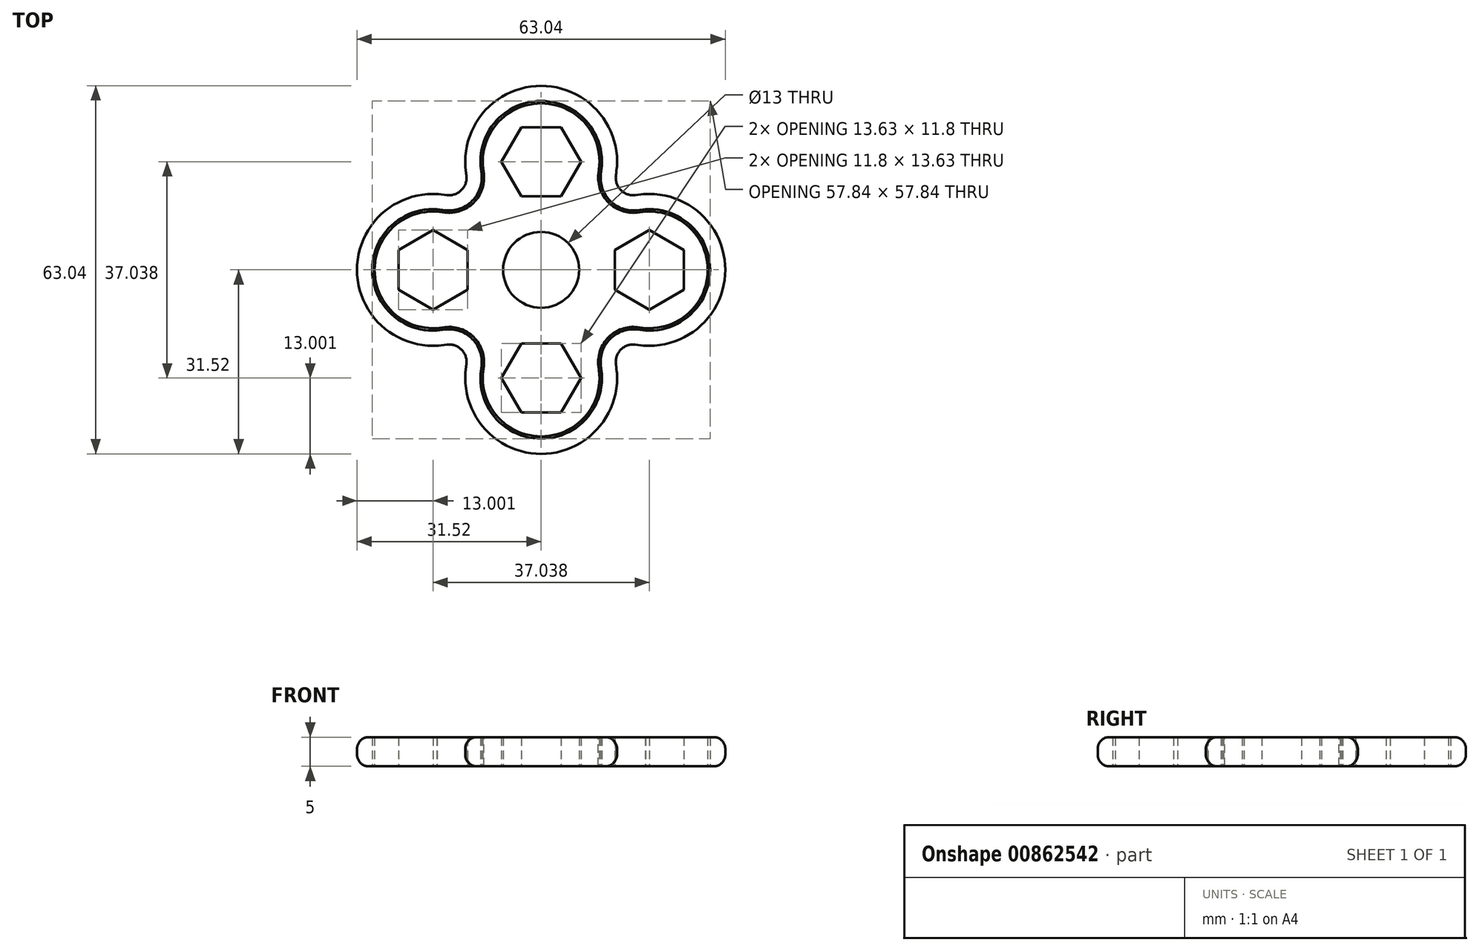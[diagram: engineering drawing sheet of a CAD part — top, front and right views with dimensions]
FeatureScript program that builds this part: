
annotation { "Feature Type Name" : "Feature", "Feature Type Description" : "" }
export const myFeature = defineFeature(function(context is Context, id is Id, definition is map)
    precondition{}
    {
        {
            var Q0;
            Q0=qCreatedBy(makeId("Top.planeOp"),FACE);
            var sketch = newSketch(context, id + "F0", { "sketchPlane" : qUnion([Q0])});
            skCircle(sketch, "E0", {"center": v(0, 0) * mm, "radius": 6.5 * mm});
            skPoint(sketch, "E1.0.midPoint", {"position": v(0, 12.5) * mm});
            skCircle(sketch, "E2.cCircle", {"center": v(0, 18.52) * mm, "radius": 10 * mm});
            skLineSegment(sketch, "E2.0", {"start": v(-5.77, 28.52) * mm, "end": v(5.77, 28.52) * mm});
            skLineSegment(sketch, "E2.1", {"start": v(5.77, 28.52) * mm, "end": v(11.55, 18.52) * mm, "construction": true});
            skLineSegment(sketch, "E2.2", {"start": v(11.55, 18.52) * mm, "end": v(5.77, 8.52) * mm, "construction": true});
            skLineSegment(sketch, "E2.3", {"start": v(5.77, 8.52) * mm, "end": v(-5.77, 8.52) * mm});
            skLineSegment(sketch, "E2.4", {"start": v(-5.77, 8.52) * mm, "end": v(-11.55, 18.52) * mm, "construction": true});
            skLineSegment(sketch, "E2.5", {"start": v(-11.55, 18.52) * mm, "end": v(-5.77, 28.52) * mm, "construction": true});
            skPoint(sketch, "E2.0.midPoint", {"position": v(0, 28.52) * mm});
            skCircle(sketch, "E3.cCircle", {"center": v(0, 18.52) * mm, "radius": 5.9 * mm, "construction": true});
            skLineSegment(sketch, "E3.0", {"start": v(-3.4, 24.42) * mm, "end": v(3.4, 24.42) * mm});
            skLineSegment(sketch, "E3.1", {"start": v(3.4, 24.42) * mm, "end": v(6.81, 18.52) * mm});
            skLineSegment(sketch, "E3.2", {"start": v(6.81, 18.52) * mm, "end": v(3.4, 12.62) * mm});
            skLineSegment(sketch, "E3.3", {"start": v(3.4, 12.62) * mm, "end": v(-3.4, 12.62) * mm});
            skLineSegment(sketch, "E3.4", {"start": v(-3.4, 12.62) * mm, "end": v(-6.81, 18.52) * mm});
            skLineSegment(sketch, "E3.5", {"start": v(-6.81, 18.52) * mm, "end": v(-3.4, 24.42) * mm});
            skPoint(sketch, "E3.0.midPoint", {"position": v(0, 24.42) * mm});
            skLineSegment(sketch, "E4", {"start": v(0, 8.52) * mm, "end": v(0, 12.5) * mm, "construction": true});
            skLineSegment(sketch, "E5", {"start": v(14.43, 0) * mm, "end": v(26.22, 0) * mm, "construction": true});
            skCircle(sketch, "E6.cCircle", {"center": v(0, 0) * mm, "radius": 12.62 * mm, "construction": true});
            skLineSegment(sketch, "E6.0", {"start": v(-5.23, 12.62) * mm, "end": v(5.23, 12.62) * mm});
            skLineSegment(sketch, "E6.1", {"start": v(5.23, 12.62) * mm, "end": v(12.62, 5.23) * mm});
            skLineSegment(sketch, "E6.2", {"start": v(12.62, 5.23) * mm, "end": v(12.62, -5.23) * mm});
            skLineSegment(sketch, "E6.3", {"start": v(12.62, -5.23) * mm, "end": v(5.23, -12.62) * mm});
            skLineSegment(sketch, "E6.4", {"start": v(5.23, -12.62) * mm, "end": v(-5.23, -12.62) * mm});
            skLineSegment(sketch, "E6.5", {"start": v(-5.23, -12.62) * mm, "end": v(-12.62, -5.23) * mm});
            skLineSegment(sketch, "E6.6", {"start": v(-12.62, -5.23) * mm, "end": v(-12.62, 5.23) * mm});
            skLineSegment(sketch, "E6.7", {"start": v(-12.62, 5.23) * mm, "end": v(-5.23, 12.62) * mm});
            skPoint(sketch, "E6.0.midPoint", {"position": v(0, 12.62) * mm});
            skLineSegment(sketch, "E7", {"start": v(-9.98, 17.86) * mm, "end": v(-8.92, 8.92) * mm});
            skLineSegment(sketch, "E8", {"start": v(8.92, 8.92) * mm, "end": v(9.98, 17.86) * mm});
            skSolve(sketch);
        }
        {
            var Q0;
            Q0=makeQuery(id+"F0.imprint","IMPRINT",FACE,{"disambiguationData":[TD([[makeQuery(id+"F0.imprint","IMPRINT",EDGE,{"derivedFrom":sQuery(id+"F0.wireOp",EDGE,"E0")}),-1.0]])]});
            var Q1;
            {var subQ1=sQuery(id+"F0.wireOp",EDGE,"E1.0");Q1=makeQuery(id+"F0.imprint","IMPRINT",FACE,{"disambiguationData":[TD([[makeQuery(id+"F0.imprint","IMPRINT",EDGE,{"derivedFrom":subQ1}),-1.0]])]});}
            extrude(context, id + "F1", {"entities" : qUnion([Q0, Q1]), "depth" : 5 * mm, "offsetDistance" : 25 * mm});
        }
        {
            var Q0;
            {var subQ5=sQuery(id+"F0.wireOp",EDGE,"E1.0");Q0=makeQuery(id+"F0.imprint","IMPRINT",FACE,{"disambiguationData":[TD([[makeQuery(id+"F0.imprint","IMPRINT",EDGE,{"derivedFrom":subQ5}),1.0]])]});}
            var Q1;
            {var subQ1=sQuery(id+"F0.wireOp",EDGE,"E1.0");Q1=makeQuery(id+"F0.imprint","IMPRINT",FACE,{"disambiguationData":[TD([[makeQuery(id+"F0.imprint","IMPRINT",EDGE,{"derivedFrom":subQ1}),-1.0]])]});}
            var Q2;
            {var subQ0=sQuery(id+"F0.wireOp",EDGE,"06393e6b-db47-430a-9c8e-1a9a39b87be70.MirrorC");var subQ1=sQuery(id+"F0.wireOp",EDGE,"E1.5");var subQ2=makeQuery(id+"F0.imprint","INTERSECT",VERTEX,{"derivedFrom":[subQ1,subQ0]});Q2=makeQuery(id+"F0.imprint","IMPRINT",FACE,{"disambiguationData":[TD([[makeQuery(id+"F0.imprint","IMPRINT",EDGE,{"disambiguationData":[TD([[subQ2,-1.0]])],"derivedFrom":subQ1}),1.0]])]});}
            var Q3;
            {var subQ0=sQuery(id+"F0.wireOp",EDGE,"rzDCEoio-iX78-1nDV-NMlx-LalMg3SrlLpn");var subQ1=sQuery(id+"F0.wireOp",EDGE,"E1.1");var subQ2=makeQuery(id+"F0.imprint","INTERSECT",VERTEX,{"derivedFrom":[subQ1,subQ0]});Q3=makeQuery(id+"F0.imprint","IMPRINT",FACE,{"disambiguationData":[TD([[makeQuery(id+"F0.imprint","IMPRINT",EDGE,{"disambiguationData":[TD([[subQ2,1.0]])],"derivedFrom":subQ1}),1.0]])]});}
            var Q4;
            Q4=makeQuery(id+"F0.imprint","IMPRINT",FACE,{"disambiguationData":[TD([[makeQuery(id+"F0.imprint","IMPRINT",EDGE,{"derivedFrom":sQuery(id+"F0.wireOp",EDGE,"E3.0")}),1.0]])]});
            var Q5;
            {var subQ0=sQuery(id+"F0.wireOp",EDGE,"E3.3");Q5=makeQuery(id+"F0.imprint","IMPRINT",FACE,{"disambiguationData":[TD([[makeQuery(id+"F0.imprint","IMPRINT",EDGE,{"derivedFrom":subQ0}),1.0]])]});}
            var Q6;
            {var subQ0=sQuery(id+"F0.wireOp",EDGE,"E7");var subQ1=sQuery(id+"F0.wireOp",EDGE,"E2.cCircle");var subQ2=makeQuery(id+"F0.imprint","INTERSECT",VERTEX,{"disambiguationData":[OD(0.0)],"derivedFrom":[subQ1,subQ0]});Q6=makeQuery(id+"F0.imprint","IMPRINT",FACE,{"disambiguationData":[TD([[makeQuery(id+"F0.imprint","IMPRINT",EDGE,{"disambiguationData":[TD([[subQ2,-1.0]])],"derivedFrom":subQ1}),-1.0]])]});}
            var Q7;
            {var subQ0=sQuery(id+"F0.wireOp",EDGE,"E6.1");var subQ1=sQuery(id+"F0.wireOp",EDGE,"E2.cCircle");var subQ2=makeQuery(id+"F0.imprint","INTERSECT",VERTEX,{"derivedFrom":[subQ1,subQ0]});Q7=makeQuery(id+"F0.imprint","IMPRINT",FACE,{"disambiguationData":[TD([[makeQuery(id+"F0.imprint","IMPRINT",EDGE,{"disambiguationData":[TD([[subQ2,-1.0]])],"derivedFrom":subQ1}),-1.0]])]});}
            extrude(context, id + "F2", {"entities" : qUnion([Q0, Q1, Q2, Q3, Q4, Q5, Q6, Q7]), "depth" : 5 * mm, "offsetDistance" : 25 * mm});
        }
        {
            var Q0;
            Q0=makeQuery(id+"F2.opExtrude","SWEPT_BODY",BODY,{"disambiguationData":[OSD([sQuery(id+"F0.wireOp",EDGE,"E2.cCircle"),sQuery(id+"F0.wireOp",EDGE,"E3.0"),sQuery(id+"F0.wireOp",EDGE,"E3.1"),sQuery(id+"F0.wireOp",EDGE,"E3.2"),sQuery(id+"F0.wireOp",EDGE,"E3.3"),sQuery(id+"F0.wireOp",EDGE,"E3.4"),sQuery(id+"F0.wireOp",EDGE,"E3.5"),sQuery(id+"F0.wireOp",EDGE,"E6.1"),sQuery(id+"F0.wireOp",EDGE,"E6.7"),sQuery(id+"F0.wireOp",EDGE,"E7"),sQuery(id+"F0.wireOp",EDGE,"E8")])]});
            var Q1;
            Q1=sQuery(id+"F0.wireOp",EDGE,"E0");
            circularPattern(context, id + "F3", {"operationType" : NewBodyOperationType.ADD, "entities" : qUnion([Q0]), "axis" : qUnion([Q1]), "angle" : 360 * degree, "instanceCount" : 4, "equalSpace" : true});
        }
        {
            var Q0;
            Q0=makeQuery(id+"F3.boolean.opBoolean","MERGE",EDGE,{"derivedFrom":[makeQuery(id+"F3.opPattern","COPY",EDGE,{"derivedFrom":makeQuery(id+"F2.opExtrude","SWEPT_EDGE",EDGE,{"disambiguationData":[OSD([sQuery(id+"F0.wireOp",EDGE,"E6.7"),sQuery(id+"F0.wireOp",EDGE,"E7")])]}),"instanceName":"1"}),makeQuery(id+"F3.opPattern","COPY",EDGE,{"derivedFrom":makeQuery(id+"F2.opExtrude","SWEPT_EDGE",EDGE,{"disambiguationData":[OSD([sQuery(id+"F0.wireOp",EDGE,"E6.1"),sQuery(id+"F0.wireOp",EDGE,"E8")])]}),"instanceName":"2"})]});
            var Q1;
            Q1=makeQuery(id+"F3.boolean.opBoolean","MERGE",EDGE,{"derivedFrom":[makeQuery(id+"F3.opPattern","COPY",EDGE,{"derivedFrom":makeQuery(id+"F2.opExtrude","SWEPT_EDGE",EDGE,{"disambiguationData":[OSD([sQuery(id+"F0.wireOp",EDGE,"E6.7"),sQuery(id+"F0.wireOp",EDGE,"E7")])]}),"instanceName":"2"}),makeQuery(id+"F3.opPattern","COPY",EDGE,{"derivedFrom":makeQuery(id+"F2.opExtrude","SWEPT_EDGE",EDGE,{"disambiguationData":[OSD([sQuery(id+"F0.wireOp",EDGE,"E6.1"),sQuery(id+"F0.wireOp",EDGE,"E8")])]}),"instanceName":"3"})]});
            var Q2;
            Q2=makeQuery(id+"F3.boolean.opBoolean","MERGE",EDGE,{"derivedFrom":[makeQuery(id+"F2.opExtrude","SWEPT_EDGE",EDGE,{"disambiguationData":[OSD([sQuery(id+"F0.wireOp",EDGE,"E6.1"),sQuery(id+"F0.wireOp",EDGE,"E8")])]}),makeQuery(id+"F3.opPattern","COPY",EDGE,{"derivedFrom":makeQuery(id+"F2.opExtrude","SWEPT_EDGE",EDGE,{"disambiguationData":[OSD([sQuery(id+"F0.wireOp",EDGE,"E6.7"),sQuery(id+"F0.wireOp",EDGE,"E7")])]}),"instanceName":"3"})]});
            var Q3;
            Q3=makeQuery(id+"F3.boolean.opBoolean","MERGE",EDGE,{"derivedFrom":[makeQuery(id+"F2.opExtrude","SWEPT_EDGE",EDGE,{"disambiguationData":[OSD([sQuery(id+"F0.wireOp",EDGE,"E6.7"),sQuery(id+"F0.wireOp",EDGE,"E7")])]}),makeQuery(id+"F3.opPattern","COPY",EDGE,{"derivedFrom":makeQuery(id+"F2.opExtrude","SWEPT_EDGE",EDGE,{"disambiguationData":[OSD([sQuery(id+"F0.wireOp",EDGE,"E6.1"),sQuery(id+"F0.wireOp",EDGE,"E8")])]}),"instanceName":"1"})]});
            fillet(context, id + "F4", {"entities" : qUnion([Q0, Q1, Q2, Q3]), "radius" : 6 * mm, "tangentPropagation" : true, "allowEdgeOverflow" : false});
        }
        {
            var Q0;
            {var subQ0=sQuery(id+"F0.wireOp",EDGE,"E6.7");var subQ1=sQuery(id+"F0.wireOp",EDGE,"E6.1");var subQ2=sQuery(id+"F0.wireOp",EDGE,"E2.cCircle");var subQ3=makeQuery(id+"F2.opExtrude","CAP_FACE",FACE,{"disambiguationData":[OSD([subQ2,sQuery(id+"F0.wireOp",EDGE,"E3.0"),sQuery(id+"F0.wireOp",EDGE,"E3.1"),sQuery(id+"F0.wireOp",EDGE,"E3.2"),sQuery(id+"F0.wireOp",EDGE,"E3.3"),sQuery(id+"F0.wireOp",EDGE,"E3.4"),sQuery(id+"F0.wireOp",EDGE,"E3.5"),subQ1,subQ0,sQuery(id+"F0.wireOp",EDGE,"E7"),sQuery(id+"F0.wireOp",EDGE,"E8")])],"isStart":true});Q0=makeQuery(id+"F3.boolean.opBoolean","MERGE",FACE,{"derivedFrom":[makeQuery(id+"F1.opExtrude","CAP_FACE",FACE,{"disambiguationData":[OSD([sQuery(id+"F0.wireOp",EDGE,"E0"),subQ2,subQ1,sQuery(id+"F0.wireOp",EDGE,"E6.2"),sQuery(id+"F0.wireOp",EDGE,"E6.3"),sQuery(id+"F0.wireOp",EDGE,"E6.4"),sQuery(id+"F0.wireOp",EDGE,"E6.5"),sQuery(id+"F0.wireOp",EDGE,"E6.6"),subQ0])],"isStart":true}),subQ3,makeQuery(id+"F3.opPattern","COPY",FACE,{"derivedFrom":subQ3,"instanceName":"1"}),makeQuery(id+"F3.opPattern","COPY",FACE,{"derivedFrom":subQ3,"instanceName":"2"}),makeQuery(id+"F3.opPattern","COPY",FACE,{"derivedFrom":subQ3,"instanceName":"3"})]});}
            var sketch = newSketch(context, id + "F5", { "sketchPlane" : qUnion([Q0])});
            skArc(sketch, "E9.0", {"start": v(12.97, 17.58) * mm, "mid": v(0, 31.52) * mm, "end": v(-12.97, 17.58) * mm});
            skLineSegment(sketch, "E9.1", {"start": v(12.8, 16.13) * mm, "end": v(12.97, 17.58) * mm});
            skArc(sketch, "E9.2", {"start": v(16.13, 12.8) * mm, "mid": v(13.65, 13.65) * mm, "end": v(12.8, 16.13) * mm});
            skLineSegment(sketch, "E9.3", {"start": v(17.58, 12.97) * mm, "end": v(16.13, 12.8) * mm});
            skArc(sketch, "E9.4", {"start": v(17.58, -12.97) * mm, "mid": v(31.52, 0) * mm, "end": v(17.58, 12.97) * mm});
            skLineSegment(sketch, "E9.5", {"start": v(-17.58, -12.97) * mm, "end": v(-16.13, -12.8) * mm});
            skArc(sketch, "E9.6", {"start": v(-17.58, 12.97) * mm, "mid": v(-31.52, 0) * mm, "end": v(-17.58, -12.97) * mm});
            skLineSegment(sketch, "E9.7", {"start": v(-16.13, 12.8) * mm, "end": v(-17.58, 12.97) * mm});
            skArc(sketch, "E9.8", {"start": v(-12.8, 16.13) * mm, "mid": v(-13.65, 13.65) * mm, "end": v(-16.13, 12.8) * mm});
            skArc(sketch, "E9.9", {"start": v(-16.13, -12.8) * mm, "mid": v(-13.65, -13.65) * mm, "end": v(-12.8, -16.13) * mm});
            skLineSegment(sketch, "E9.10", {"start": v(-12.8, -16.13) * mm, "end": v(-12.97, -17.58) * mm});
            skArc(sketch, "E9.11", {"start": v(-12.97, -17.58) * mm, "mid": v(0, -31.52) * mm, "end": v(12.97, -17.58) * mm});
            skLineSegment(sketch, "E9.12", {"start": v(12.97, -17.58) * mm, "end": v(12.8, -16.13) * mm});
            skArc(sketch, "E9.13", {"start": v(12.8, -16.13) * mm, "mid": v(13.65, -13.65) * mm, "end": v(16.13, -12.8) * mm});
            skLineSegment(sketch, "E9.14", {"start": v(-12.97, 17.58) * mm, "end": v(-12.8, 16.13) * mm});
            skLineSegment(sketch, "E9.15", {"start": v(16.13, -12.8) * mm, "end": v(17.58, -12.97) * mm});
            skArc(sketch, "E10.0", {"start": v(10.38, 17.82) * mm, "mid": v(0, 28.92) * mm, "end": v(-10.38, 17.82) * mm});
            skLineSegment(sketch, "E10.1", {"start": v(10.21, 16.43) * mm, "end": v(10.38, 17.82) * mm});
            skArc(sketch, "E10.2", {"start": v(16.43, 10.21) * mm, "mid": v(11.81, 11.81) * mm, "end": v(10.21, 16.43) * mm});
            skLineSegment(sketch, "E10.3", {"start": v(17.82, 10.38) * mm, "end": v(16.43, 10.21) * mm});
            skArc(sketch, "E10.4", {"start": v(17.82, -10.38) * mm, "mid": v(28.92, 0) * mm, "end": v(17.82, 10.38) * mm});
            skLineSegment(sketch, "E10.5", {"start": v(-17.82, -10.38) * mm, "end": v(-16.43, -10.21) * mm});
            skArc(sketch, "E10.6", {"start": v(-17.82, 10.38) * mm, "mid": v(-28.92, 0) * mm, "end": v(-17.82, -10.38) * mm});
            skLineSegment(sketch, "E10.7", {"start": v(-16.43, 10.21) * mm, "end": v(-17.82, 10.38) * mm});
            skArc(sketch, "E10.8", {"start": v(-10.21, 16.43) * mm, "mid": v(-11.81, 11.81) * mm, "end": v(-16.43, 10.21) * mm});
            skArc(sketch, "E10.9", {"start": v(-16.43, -10.21) * mm, "mid": v(-11.81, -11.81) * mm, "end": v(-10.21, -16.43) * mm});
            skLineSegment(sketch, "E10.10", {"start": v(-10.21, -16.43) * mm, "end": v(-10.38, -17.82) * mm});
            skArc(sketch, "E10.11", {"start": v(-10.38, -17.82) * mm, "mid": v(0, -28.92) * mm, "end": v(10.38, -17.82) * mm});
            skLineSegment(sketch, "E10.12", {"start": v(10.38, -17.82) * mm, "end": v(10.21, -16.43) * mm});
            skArc(sketch, "E10.13", {"start": v(10.21, -16.43) * mm, "mid": v(11.81, -11.81) * mm, "end": v(16.43, -10.21) * mm});
            skLineSegment(sketch, "E10.14", {"start": v(-10.38, 17.82) * mm, "end": v(-10.21, 16.43) * mm});
            skLineSegment(sketch, "E10.15", {"start": v(16.43, -10.21) * mm, "end": v(17.82, -10.38) * mm});
            skSolve(sketch);
        }
        {
            var Q0;
            Q0=makeQuery(id+"F5.imprint","IMPRINT",FACE,{"disambiguationData":[TD([[makeQuery(id+"F5.imprint","IMPRINT",EDGE,{"derivedFrom":sQuery(id+"F5.wireOp",EDGE,"E9.0")}),1.0]])]});
            extrude(context, id + "F6", {"entities" : qUnion([Q0]), "oppositeDirection" : true, "depth" : 5 * mm, "offsetDistance" : 25 * mm});
        }
        {
            var Q0;
            Q0=makeQuery(id+"F6.opExtrude","SWEPT_FACE",FACE,{"disambiguationData":[OSD([sQuery(id+"F5.wireOp",EDGE,"E9.11")])]});
            var Q1;
            Q1=makeQuery(id+"F6.opExtrude","SWEPT_FACE",FACE,{"disambiguationData":[OSD([sQuery(id+"F5.wireOp",EDGE,"E9.5")])]});
            var Q2;
            Q2=makeQuery(id+"F6.opExtrude","SWEPT_FACE",FACE,{"disambiguationData":[OSD([sQuery(id+"F5.wireOp",EDGE,"E9.6")])]});
            var Q3;
            Q3=makeQuery(id+"F6.opExtrude","SWEPT_EDGE",EDGE,{"disambiguationData":[OSD([sQuery(id+"F5.wireOp",EDGE,"E9.10"),sQuery(id+"F5.wireOp",EDGE,"E9.11")])]});
            var Q4;
            Q4=makeQuery(id+"F6.opExtrude","SWEPT_FACE",FACE,{"disambiguationData":[OSD([sQuery(id+"F5.wireOp",EDGE,"E9.10")])]});
            var Q5;
            Q5=makeQuery(id+"F6.opExtrude","SWEPT_FACE",FACE,{"disambiguationData":[OSD([sQuery(id+"F5.wireOp",EDGE,"E9.9")])]});
            var Q6;
            Q6=makeQuery(id+"F6.opExtrude","SWEPT_FACE",FACE,{"disambiguationData":[OSD([sQuery(id+"F5.wireOp",EDGE,"E9.8")])]});
            var Q7;
            Q7=makeQuery(id+"F6.opExtrude","SWEPT_EDGE",EDGE,{"disambiguationData":[OSD([sQuery(id+"F5.wireOp",EDGE,"E9.0"),sQuery(id+"F5.wireOp",EDGE,"E9.14")])]});
            var Q8;
            Q8=makeQuery(id+"F6.opExtrude","SWEPT_FACE",FACE,{"disambiguationData":[OSD([sQuery(id+"F5.wireOp",EDGE,"E9.0")])]});
            var Q9;
            Q9=makeQuery(id+"F6.opExtrude","SWEPT_FACE",FACE,{"disambiguationData":[OSD([sQuery(id+"F5.wireOp",EDGE,"E9.14")])]});
            var Q10;
            Q10=makeQuery(id+"F6.opExtrude","SWEPT_FACE",FACE,{"disambiguationData":[OSD([sQuery(id+"F5.wireOp",EDGE,"E9.1")])]});
            var Q11;
            Q11=makeQuery(id+"F6.opExtrude","SWEPT_FACE",FACE,{"disambiguationData":[OSD([sQuery(id+"F5.wireOp",EDGE,"E9.2")])]});
            var Q12;
            Q12=makeQuery(id+"F6.opExtrude","SWEPT_FACE",FACE,{"disambiguationData":[OSD([sQuery(id+"F5.wireOp",EDGE,"E9.3")])]});
            var Q13;
            Q13=makeQuery(id+"F6.opExtrude","SWEPT_FACE",FACE,{"disambiguationData":[OSD([sQuery(id+"F5.wireOp",EDGE,"E9.4")])]});
            var Q14;
            Q14=makeQuery(id+"F6.opExtrude","SWEPT_FACE",FACE,{"disambiguationData":[OSD([sQuery(id+"F5.wireOp",EDGE,"E9.15")])]});
            var Q15;
            Q15=makeQuery(id+"F6.opExtrude","SWEPT_FACE",FACE,{"disambiguationData":[OSD([sQuery(id+"F5.wireOp",EDGE,"E9.13")])]});
            var Q16;
            Q16=makeQuery(id+"F6.opExtrude","SWEPT_FACE",FACE,{"disambiguationData":[OSD([sQuery(id+"F5.wireOp",EDGE,"E9.12")])]});
            var Q17;
            Q17=makeQuery(id+"F6.opExtrude","SWEPT_FACE",FACE,{"disambiguationData":[OSD([sQuery(id+"F5.wireOp",EDGE,"E9.7")])]});
            fillet(context, id + "F7", {"entities" : qUnion([Q0, Q1, Q2, Q3, Q4, Q5, Q6, Q7, Q8, Q9, Q10, Q11, Q12, Q13, Q14, Q15, Q16, Q17]), "radius" : 2 * mm, "tangentPropagation" : true, "allowEdgeOverflow" : false});
        }
    });
